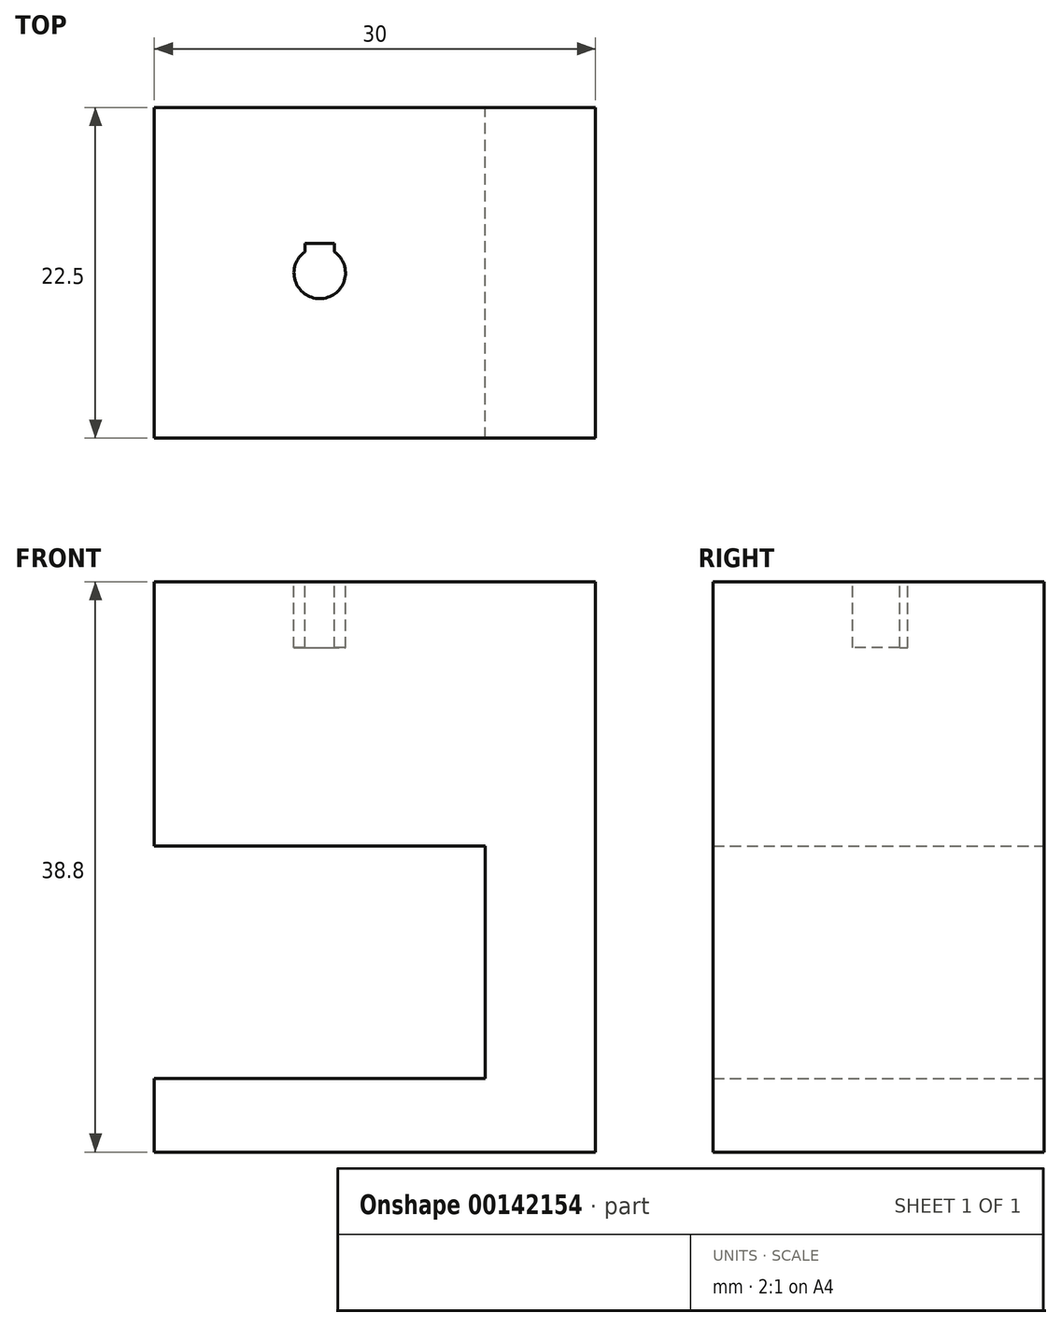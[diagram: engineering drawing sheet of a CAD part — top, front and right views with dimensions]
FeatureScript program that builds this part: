
annotation { "Feature Type Name" : "Feature", "Feature Type Description" : "" }
export const myFeature = defineFeature(function(context is Context, id is Id, definition is map)
    precondition{}
    {
        {
            var Q0;
            Q0=qCreatedBy(makeId("Front.planeOp"),FACE);
            var sketch = newSketch(context, id + "F0", { "sketchPlane" : qUnion([Q0])});
            skLineSegment(sketch, "E0", {"start": v(-15, 15.3) * mm, "end": v(15, 15.3) * mm});
            skLineSegment(sketch, "E1", {"start": v(15, 15.3) * mm, "end": v(15, -23.5) * mm});
            skLineSegment(sketch, "E2", {"start": v(15, -23.5) * mm, "end": v(-15, -23.5) * mm});
            skLineSegment(sketch, "E3", {"start": v(-15, -23.5) * mm, "end": v(-15, -18.5) * mm});
            skLineSegment(sketch, "E4", {"start": v(-15, -18.5) * mm, "end": v(7.5, -18.5) * mm});
            skLineSegment(sketch, "E5", {"start": v(7.5, -18.5) * mm, "end": v(7.5, -2.7) * mm});
            skLineSegment(sketch, "E6", {"start": v(7.5, -2.7) * mm, "end": v(-15, -2.7) * mm});
            skLineSegment(sketch, "E7", {"start": v(-15, -2.7) * mm, "end": v(-15, 15.3) * mm});
            skSolve(sketch);
        }
        {
            var Q0;
            Q0=makeQuery(id+"F0.imprint","IMPRINT",FACE,{"disambiguationData":[TD([[makeQuery(id+"F0.imprint","IMPRINT",EDGE,{"derivedFrom":sQuery(id+"F0.wireOp",EDGE,"E0")}),-1.0]])]});
            extrude(context, id + "F1", {"entities" : qUnion([Q0]), "depth" : 22.5 * mm});
        }
        {
            var Q0;
            Q0=makeQuery(id+"F1.opExtrude","SWEPT_FACE",FACE,{"disambiguationData":[OSD([sQuery(id+"F0.wireOp",EDGE,"E0")])]});
            var sketch = newSketch(context, id + "F2", { "sketchPlane" : qUnion([Q0])});
            skPoint(sketch, "E8.centerSnap0", {"position": v(-15, -11.25) * mm});
            skPoint(sketch, "E8.centerSnap1", {"position": v(0, 0) * mm});
            skArc(sketch, "E9", {"start": v(-4.75, -9.81) * mm, "mid": v(-3.75, -13) * mm, "end": v(-2.75, -9.81) * mm});
            skLineSegment(sketch, "E10.top", {"start": v(-4.75, -9.25) * mm, "end": v(-2.75, -9.25) * mm});
            skLineSegment(sketch, "E10.left", {"start": v(-4.75, -9.81) * mm, "end": v(-4.75, -9.25) * mm});
            skLineSegment(sketch, "E10.right", {"start": v(-2.75, -9.81) * mm, "end": v(-2.75, -9.25) * mm});
            skLineSegment(sketch, "E11", {"start": v(-15, -11.25) * mm, "end": v(-3.75, -11.25) * mm, "construction": true});
            skSolve(sketch);
        }
        {
            var Q0;
            Q0=qSketchRegion(id+"F2",true);
            extrude(context, id + "F3", {"entities" : qUnion([Q0]), "operationType" : NewBodyOperationType.REMOVE, "oppositeDirection" : true, "depth" : 4.5 * mm});
        }
    });
